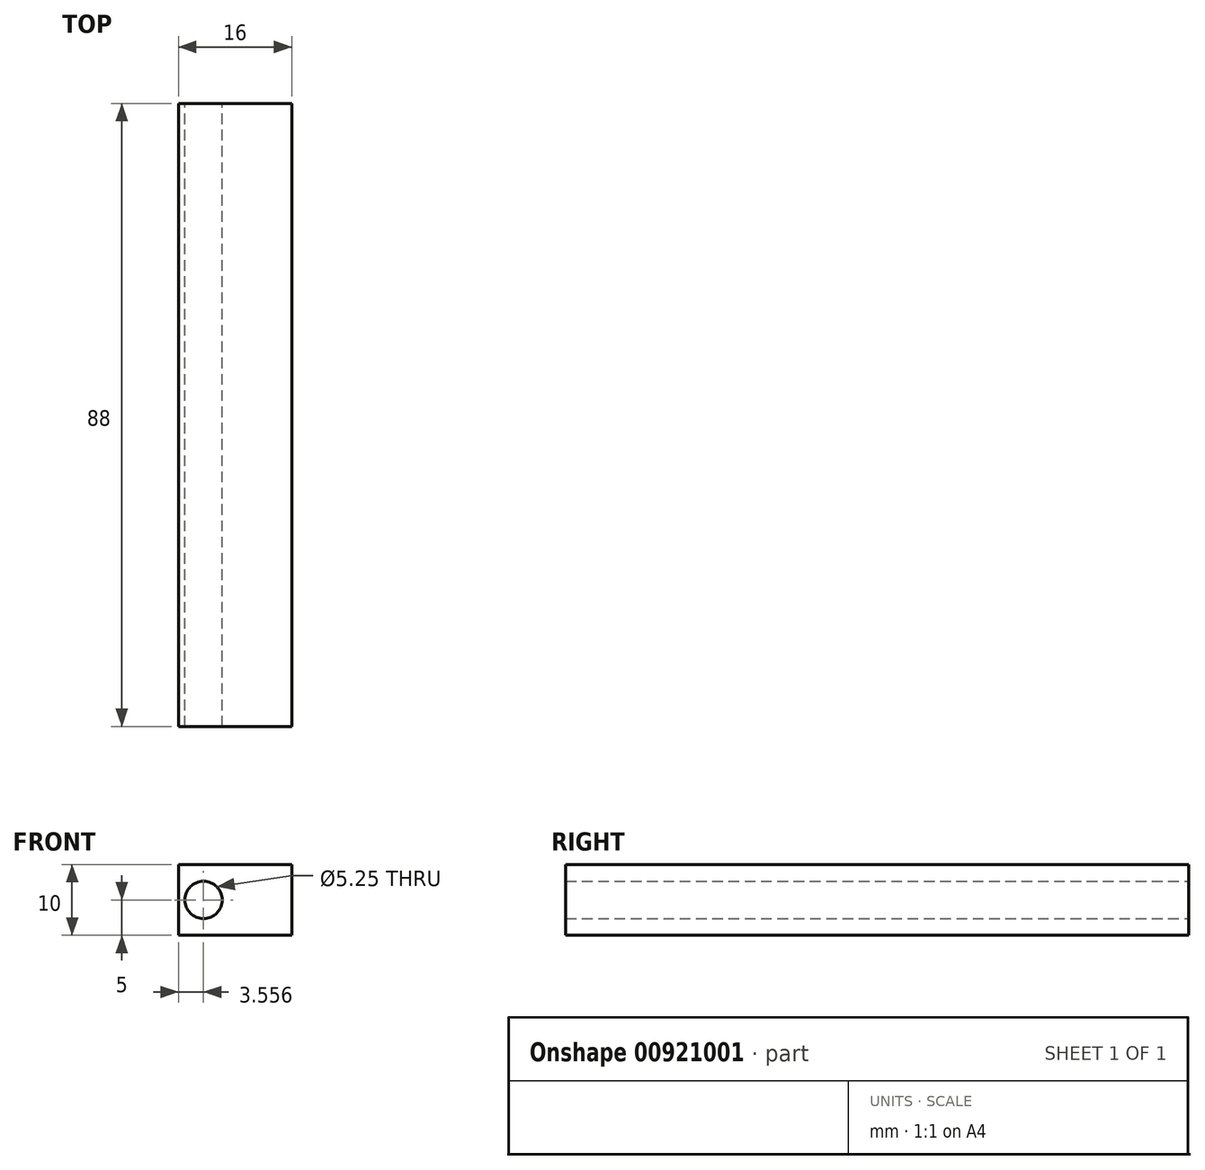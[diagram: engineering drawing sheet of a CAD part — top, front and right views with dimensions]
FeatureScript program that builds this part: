
annotation { "Feature Type Name" : "Feature", "Feature Type Description" : "" }
export const myFeature = defineFeature(function(context is Context, id is Id, definition is map)
    precondition{}
    {
        {
            var Q0;
            Q0=qCreatedBy(makeId("Front.planeOp"),FACE);
            var sketch = newSketch(context, id + "F0", { "sketchPlane" : qUnion([Q0])});
            skLineSegment(sketch, "E0.bottom", {"start": v(8, -5) * mm, "end": v(-8, -5) * mm});
            skLineSegment(sketch, "E0.top", {"start": v(8, 5) * mm, "end": v(-8, 5) * mm});
            skLineSegment(sketch, "E0.left", {"start": v(8, -5) * mm, "end": v(8, 5) * mm});
            skLineSegment(sketch, "E0.right", {"start": v(-8, -5) * mm, "end": v(-8, 5) * mm});
            skPoint(sketch, "E0.middle", {"position": v(0, 0) * mm});
            skCircle(sketch, "E1", {"center": v(-4.44, 0) * mm, "radius": 2.62 * mm});
            skSolve(sketch);
        }
        {
            var Q0;
            Q0=makeQuery(id+"F0.imprint","IMPRINT",FACE,{"disambiguationData":[TD([[makeQuery(id+"F0.imprint","IMPRINT",EDGE,{"derivedFrom":sQuery(id+"F0.wireOp",EDGE,"E0.bottom")}),-1.0]])]});
            extrude(context, id + "F1", {"entities" : qUnion([Q0]), "depth" : 88 * mm, "offsetDistance" : 25 * mm});
        }
    });
